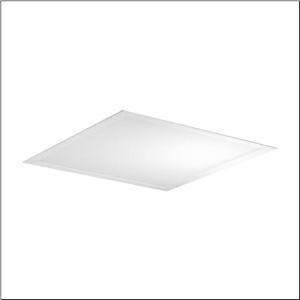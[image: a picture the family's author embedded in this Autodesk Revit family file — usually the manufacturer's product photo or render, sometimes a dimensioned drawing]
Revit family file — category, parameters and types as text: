
# Revit family: apollon_r__31_square_51mp11w72442_ea88
name_source: partatom
category: Lighting Fixtures
units: mm (PartAtom-declared; Revit-internal decimal feet)

## family parameters
Cut with Voids When Loaded = No
Host = Face
Light Source = No
Part Type = Normal
Room Calculation Point = No
Round Connector Dimension = Use Diameter
Shared = No

## types (1)
- Apollon® 31 square (1 x LED, 4000 lm, 27.5 W, 4000K)
    Apparent Load = 28 VA
    CIE Flux Codes = 61 87 97 100 100
    Color Rendering = 80
    Color Temperature = 4000K
    Default Elevation = 1800 mm
    Description = Apollon® 31 square, office luminaire, primary optical cover: micro prismatic cover, of PMMA, CAT 2 (L<= 3000cd/m²), light emission: direct distribution, primary light characteristic: symmetric, installation type: lay-in mounting, LED, rated luminous flux: 4.000lm, luminous efficacy: 145lm/W, light colour: 840, colour temperature: 4000K, with terminal, 3-pole, mains connection: 220..240V, AC, 50/60Hz, rated input power: 28W, housing, of aluminium, traffic white (RAL 9016), module: M625, length: 620mm, width: 620mm, height: 32mm, housing upper side, of sheet steel, galvanised, protection rating (complete): IP20, protection rating (on room side): IP40, insulation class (complete): insulation class II (safety insulation), certification: CE, ENEC, impact resistance: IK03, permissible operating ambient temperature: -20..+40°C, permissible storage temperature: -20..+60°C, packaging unit: 1 piece
    Height = 0 mm  [stored 0 ft]
    Lamp = 1 x LED
    Lamp Light Flux = 4000 lm
    Lamp Power = 27.5 W
    Lamp count = 1
    Length = 620 mm
    Luminous efficacy = 145 lm/W
    Manufacturer = Siteco
    ModVariant = No
    Model = 51MP11W72442
    Mounting Place = Ceiling
    Mounting Type = Recessed
    Number of Poles = 1
    OnlyDefault = Yes
    Power Factor = 1
    Product Name = Apollon® 31 square
    Product group = office luminaire | ceiling recessed
    ProductGroupID = 401
    Protection Class = Protection class II
    Protection Degree = IP 20
    RLX_Detail_Level = 1
    RLX_Emergency_Light_Flux = 0 lm
    RLX_Emergency_Type = 0
    RLX_Emergency_Type_DB = No
    RlxData = <blob elided: 12937 chars, md5=a956d047>
    Socket = socket
    Standby Power = 0 W
    System Light Flux = 4000 lm
    System Power = 28 W
    Type Comments = Product without accessories
    Type Image = l_1291039.jpg
    URL = http://relux.com
    VarID = ---
    Voltage = 0 V
    Weight = 0.00 kg
    Width = 620 mm

note: [stored X ft] marks values corroborated as IEEE doubles in the binary element streams (Revit-internal decimal feet)

## geometry (parser evidence)
native form markers: Sweep x10
no freeform markers — native parametric forms only
